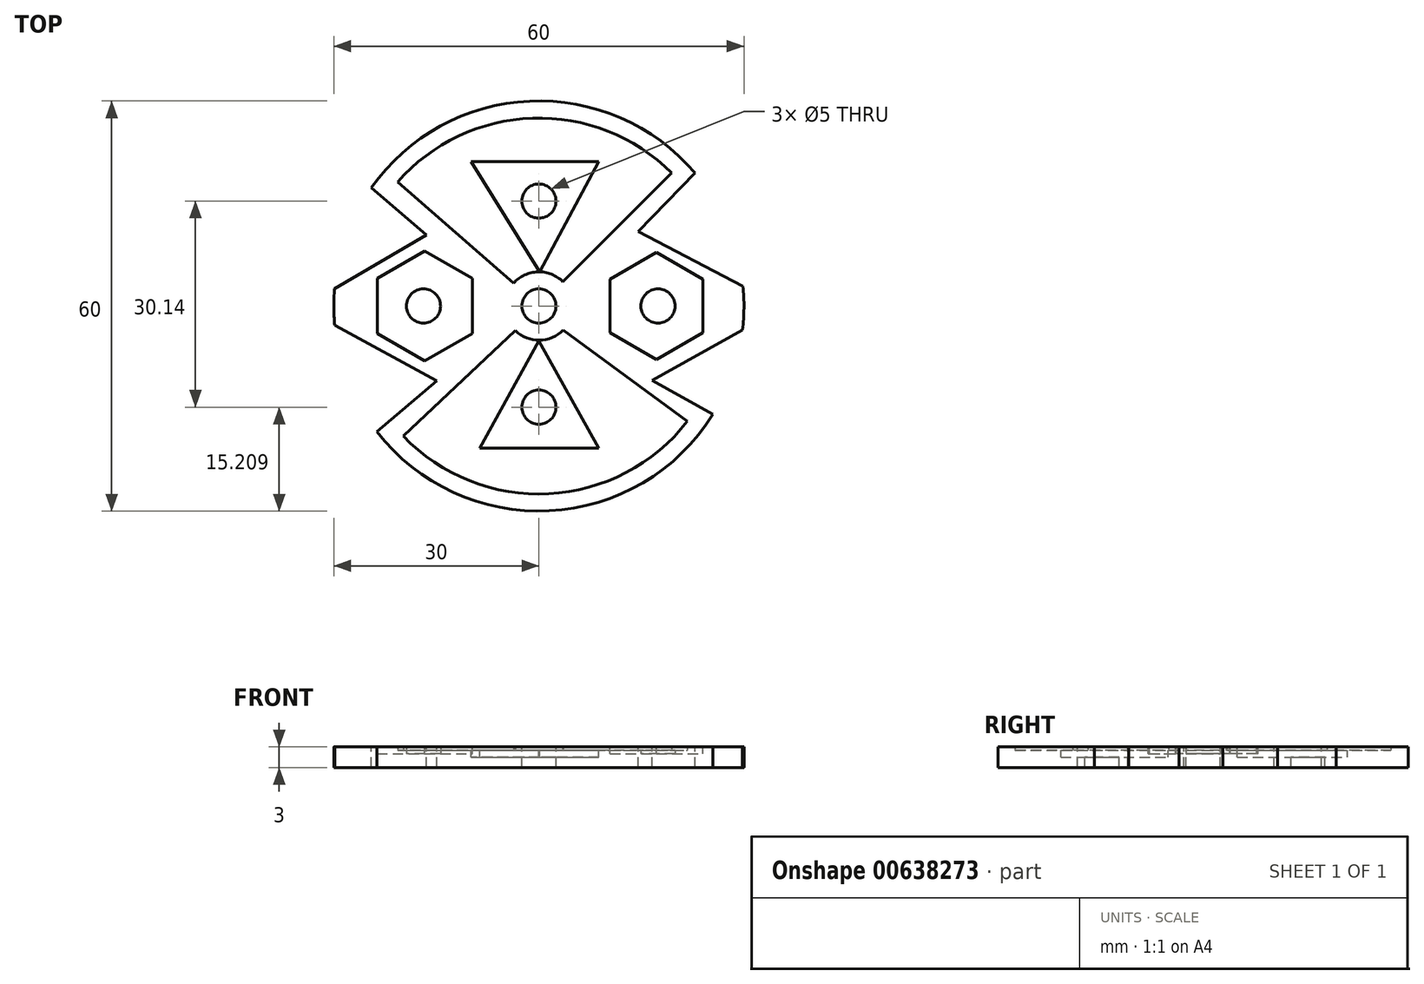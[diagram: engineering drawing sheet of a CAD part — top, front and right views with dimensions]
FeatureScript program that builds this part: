
annotation { "Feature Type Name" : "Feature", "Feature Type Description" : "" }
export const myFeature = defineFeature(function(context is Context, id is Id, definition is map)
    precondition{}
    {
        {
            var Q0;
            Q0=qCreatedBy(makeId("Top.planeOp"),FACE);
            var sketch = newSketch(context, id + "F0", { "sketchPlane" : qUnion([Q0])});
            skCircle(sketch, "E0", {"center": v(0, 0) * mm, "radius": 30 * mm});
            skSolve(sketch);
        }
        {
            var Q0;
            Q0=makeQuery(id+"F0.imprint","IMPRINT",FACE,{"disambiguationData":[TD([[makeQuery(id+"F0.imprint","IMPRINT",EDGE,{"derivedFrom":sQuery(id+"F0.wireOp",EDGE,"E0")}),1.0]])]});
            extrude(context, id + "F1", {"entities" : qUnion([Q0]), "depth" : 3 * mm, "offsetDistance" : 25 * mm});
        }
        {
            var Q0;
            Q0=makeQuery(id+"F1.opExtrude","CAP_FACE",FACE,{"disambiguationData":[OSD([sQuery(id+"F0.wireOp",EDGE,"E0")])],"isStart":false});
            var sketch = newSketch(context, id + "F2", { "sketchPlane" : qUnion([Q0])});
            skCircle(sketch, "E1", {"center": v(0, 0) * mm, "radius": 2.5 * mm});
            skSolve(sketch);
        }
        {
            var Q0;
            Q0=sQuery(id+"F2.wireOp",VERTEX,"E1.center");
            var Q1;
            Q1=makeQuery(id+"F1.opExtrude","SWEPT_BODY",BODY,{"disambiguationData":[OSD([sQuery(id+"F0.wireOp",EDGE,"E0")])]});
            hole(context, id + "F3", {"style" : HoleStyle.SIMPLE, "endStyle" : HoleEndStyle.THROUGH, "holeDiameter" : 5 * mm, "majorDiameter" : 5 * mm, "isTappedThrough" : true, "tappedDepth" : 12 * mm, "tapClearance" : 3, "locations" : qUnion([Q0]), "scope" : qUnion([Q1])});
        }
        {
            var Q0;
            Q0=makeQuery(id+"F1.opExtrude","CAP_FACE",FACE,{"disambiguationData":[OSD([sQuery(id+"F0.wireOp",EDGE,"E0")])],"isStart":false});
            shell(context, id + "F4", {"entities" : qUnion([Q0]), "thickness" : 2.5 * mm});
        }
        {
            var Q0;
            {var subQ0=sQuery(id+"F0.wireOp",EDGE,"E0");Q0=makeQuery(id+"F4.opShell","OFFSET_FACE",FACE,{"disambiguationData":[OSD([subQ0]),TDD([makeQuery(id+"F1.opExtrude","CAP_FACE",FACE,{"disambiguationData":[OSD([subQ0])],"isStart":true})])]});}
            var sketch = newSketch(context, id + "F5", { "sketchPlane" : qUnion([Q0])});
            skLineSegment(sketch, "E2", {"start": v(-20.67, 18.14) * mm, "end": v(-3.7, 3.36) * mm});
            skLineSegment(sketch, "E3", {"start": v(3.51, 3.56) * mm, "end": v(19.42, 19.48) * mm});
            skLineSegment(sketch, "E4", {"start": v(-3.47, -3.6) * mm, "end": v(-19.84, -19.04) * mm});
            skLineSegment(sketch, "E5", {"start": v(3.58, -3.5) * mm, "end": v(21.73, -16.86) * mm});
            skSolve(sketch);
        }
        {
            var Q0;
            {var subQ0=sQuery(id+"F5.wireOp",EDGE,"E2");Q0=makeQuery(id+"F5.imprint","IMPRINT",FACE,{"disambiguationData":[TD([[makeQuery(id+"F5.imprint","IMPRINT",EDGE,{"derivedFrom":subQ0}),-1.0]])]});}
            var Q1;
            {var subQ0=sQuery(id+"F5.wireOp",EDGE,"E3");Q1=makeQuery(id+"F5.imprint","IMPRINT",FACE,{"disambiguationData":[TD([[makeQuery(id+"F5.imprint","IMPRINT",EDGE,{"derivedFrom":subQ0}),-1.0]])]});}
            extrude(context, id + "F6", {"entities" : qUnion([Q0, Q1]), "operationType" : NewBodyOperationType.ADD, "depth" : 0.5 * mm, "offsetDistance" : 25 * mm});
        }
        {
            var Q0;
            {var subQ0=sQuery(id+"F3.hole-0.sketch.wireOp",EDGE,"core_line_2");var subQ1=sQuery(id+"F0.wireOp",EDGE,"E0");var subQ2=makeQuery(id+"F1.opExtrude","CAP_FACE",FACE,{"disambiguationData":[OSD([subQ1])],"isStart":false});Q0=makeQuery(id+"F6.boolean.opBoolean","MERGE",FACE,{"derivedFrom":[makeQuery(id+"F4.opShell","OFFSET_FACE",FACE,{"disambiguationData":[OSD([subQ1]),TDD([subQ2])]}),subQ2,makeQuery(id+"F6.opExtrude","CAP_FACE",FACE,{"disambiguationData":[OSD([subQ1,subQ0,sQuery(id+"F5.wireOp",EDGE,"E2"),sQuery(id+"F5.wireOp",EDGE,"E4")])],"isStart":false}),makeQuery(id+"F6.opExtrude","CAP_FACE",FACE,{"disambiguationData":[OSD([subQ1,subQ0,sQuery(id+"F5.wireOp",EDGE,"E3"),sQuery(id+"F5.wireOp",EDGE,"E5")])],"isStart":false})]});}
            var sketch = newSketch(context, id + "F7", { "sketchPlane" : qUnion([Q0])});
            skCircle(sketch, "E6.cCircle", {"center": v(-16.7, 0) * mm, "radius": 6.96 * mm, "construction": true});
            skLineSegment(sketch, "E6.0", {"start": v(-9.75, 4.02) * mm, "end": v(-9.75, -4.02) * mm});
            skLineSegment(sketch, "E6.1", {"start": v(-9.75, -4.02) * mm, "end": v(-16.7, -8.03) * mm});
            skLineSegment(sketch, "E6.2", {"start": v(-16.7, -8.03) * mm, "end": v(-23.66, -4.02) * mm});
            skLineSegment(sketch, "E6.3", {"start": v(-23.66, -4.02) * mm, "end": v(-23.66, 4.02) * mm});
            skLineSegment(sketch, "E6.4", {"start": v(-23.66, 4.02) * mm, "end": v(-16.7, 8.03) * mm});
            skLineSegment(sketch, "E6.5", {"start": v(-16.7, 8.03) * mm, "end": v(-9.75, 4.02) * mm});
            skPoint(sketch, "E6.0.midPoint", {"position": v(-9.75, 0) * mm});
            skCircle(sketch, "E7.cCircle", {"center": v(17.2, 0) * mm, "radius": 6.78 * mm, "construction": true});
            skLineSegment(sketch, "E7.0", {"start": v(23.98, 3.91) * mm, "end": v(23.98, -3.91) * mm});
            skLineSegment(sketch, "E7.1", {"start": v(23.98, -3.91) * mm, "end": v(17.2, -7.83) * mm});
            skLineSegment(sketch, "E7.2", {"start": v(17.2, -7.83) * mm, "end": v(10.42, -3.91) * mm});
            skLineSegment(sketch, "E7.3", {"start": v(10.42, -3.91) * mm, "end": v(10.42, 3.91) * mm});
            skLineSegment(sketch, "E7.4", {"start": v(10.42, 3.91) * mm, "end": v(17.2, 7.83) * mm});
            skLineSegment(sketch, "E7.5", {"start": v(17.2, 7.83) * mm, "end": v(23.98, 3.91) * mm});
            skPoint(sketch, "E7.0.midPoint", {"position": v(23.98, 0) * mm});
            skSolve(sketch);
        }
        {
            var Q0;
            Q0=makeQuery(id+"F7.imprint","IMPRINT",FACE,{"disambiguationData":[TD([[makeQuery(id+"F7.imprint","IMPRINT",EDGE,{"derivedFrom":sQuery(id+"F7.wireOp",EDGE,"E6.0")}),-1.0]])]});
            var Q1;
            Q1=makeQuery(id+"F7.imprint","IMPRINT",FACE,{"disambiguationData":[TD([[makeQuery(id+"F7.imprint","IMPRINT",EDGE,{"derivedFrom":sQuery(id+"F7.wireOp",EDGE,"E7.0")}),-1.0]])]});
            extrude(context, id + "F8", {"entities" : qUnion([Q0, Q1]), "operationType" : NewBodyOperationType.REMOVE, "oppositeDirection" : true, "depth" : 1 * mm, "offsetDistance" : 25 * mm});
        }
        {
            var Q0;
            Q0=makeQuery(id+"F8.boolean.opBoolean","COPY",FACE,{"derivedFrom":makeQuery(id+"F8.opExtrude","CAP_FACE",FACE,{"disambiguationData":[OSD([sQuery(id+"F7.wireOp",EDGE,"E6.0"),sQuery(id+"F7.wireOp",EDGE,"E6.1"),sQuery(id+"F7.wireOp",EDGE,"E6.2"),sQuery(id+"F7.wireOp",EDGE,"E6.3"),sQuery(id+"F7.wireOp",EDGE,"E6.4"),sQuery(id+"F7.wireOp",EDGE,"E6.5")])],"isStart":false})});
            var sketch = newSketch(context, id + "F9", { "sketchPlane" : qUnion([Q0])});
            skCircle(sketch, "E8", {"center": v(-16.88, 0) * mm, "radius": 2.5 * mm});
            skSolve(sketch);
        }
        {
            var Q0;
            Q0=makeQuery(id+"F9.imprint","IMPRINT",FACE,{"disambiguationData":[TD([[makeQuery(id+"F9.imprint","IMPRINT",EDGE,{"derivedFrom":sQuery(id+"F9.wireOp",EDGE,"E8")}),1.0]])]});
            extrude(context, id + "F10", {"entities" : qUnion([Q0]), "operationType" : NewBodyOperationType.ADD, "depth" : 1 * mm, "offsetDistance" : 25 * mm});
        }
        {
            var Q0;
            Q0=makeQuery(id+"F8.boolean.opBoolean","COPY",FACE,{"derivedFrom":makeQuery(id+"F8.opExtrude","CAP_FACE",FACE,{"disambiguationData":[OSD([sQuery(id+"F7.wireOp",EDGE,"E7.0"),sQuery(id+"F7.wireOp",EDGE,"E7.1"),sQuery(id+"F7.wireOp",EDGE,"E7.2"),sQuery(id+"F7.wireOp",EDGE,"E7.3"),sQuery(id+"F7.wireOp",EDGE,"E7.4"),sQuery(id+"F7.wireOp",EDGE,"E7.5")])],"isStart":false})});
            var sketch = newSketch(context, id + "F11", { "sketchPlane" : qUnion([Q0])});
            skCircle(sketch, "E9", {"center": v(17.42, 0) * mm, "radius": 2.5 * mm});
            skSolve(sketch);
        }
        {
            var Q0;
            Q0=makeQuery(id+"F11.imprint","IMPRINT",FACE,{"disambiguationData":[TD([[makeQuery(id+"F11.imprint","IMPRINT",EDGE,{"derivedFrom":sQuery(id+"F11.wireOp",EDGE,"E9")}),1.0]])]});
            extrude(context, id + "F12", {"entities" : qUnion([Q0]), "operationType" : NewBodyOperationType.ADD, "depth" : 0.5 * mm, "offsetDistance" : 25 * mm});
        }
        {
            var Q0;
            {var subQ0=sQuery(id+"F3.hole-0.sketch.wireOp",EDGE,"core_line_2");var subQ1=sQuery(id+"F0.wireOp",EDGE,"E0");var subQ2=makeQuery(id+"F1.opExtrude","CAP_FACE",FACE,{"disambiguationData":[OSD([subQ1])],"isStart":false});Q0=makeQuery(id+"F6.boolean.opBoolean","MERGE",FACE,{"derivedFrom":[makeQuery(id+"F4.opShell","OFFSET_FACE",FACE,{"disambiguationData":[OSD([subQ1]),TDD([subQ2])]}),subQ2,makeQuery(id+"F6.opExtrude","CAP_FACE",FACE,{"disambiguationData":[OSD([subQ1,subQ0,sQuery(id+"F5.wireOp",EDGE,"E2"),sQuery(id+"F5.wireOp",EDGE,"E4")])],"isStart":false}),makeQuery(id+"F6.opExtrude","CAP_FACE",FACE,{"disambiguationData":[OSD([subQ1,subQ0,sQuery(id+"F5.wireOp",EDGE,"E3"),sQuery(id+"F5.wireOp",EDGE,"E5")])],"isStart":false})]});}
            var sketch = newSketch(context, id + "F13", { "sketchPlane" : qUnion([Q0])});
            skLineSegment(sketch, "E10", {"start": v(-24.5, 17.3) * mm, "end": v(-16.47, 10.4) * mm});
            skLineSegment(sketch, "E11", {"start": v(-16.47, 10.4) * mm, "end": v(-29.9, 2.53) * mm});
            skLineSegment(sketch, "E12", {"start": v(-23.72, -18.36) * mm, "end": v(-14.93, -10.97) * mm});
            skLineSegment(sketch, "E13", {"start": v(-14.93, -10.97) * mm, "end": v(-29.87, -2.81) * mm});
            skLineSegment(sketch, "E14", {"start": v(22.82, 19.48) * mm, "end": v(14.54, 10.89) * mm});
            skLineSegment(sketch, "E15", {"start": v(14.54, 10.89) * mm, "end": v(29.86, 2.9) * mm});
            skLineSegment(sketch, "E16", {"start": v(25.46, -15.86) * mm, "end": v(16.56, -10.88) * mm});
            skLineSegment(sketch, "E17", {"start": v(16.56, -10.88) * mm, "end": v(29.8, -3.5) * mm});
            skSolve(sketch);
        }
        {
            var Q0;
            {var subQ0=sQuery(id+"F13.wireOp",EDGE,"E10");Q0=makeQuery(id+"F13.imprint","IMPRINT",FACE,{"disambiguationData":[TD([[makeQuery(id+"F13.imprint","IMPRINT",EDGE,{"derivedFrom":subQ0}),-1.0]])]});}
            var Q1;
            {var subQ0=sQuery(id+"F13.wireOp",EDGE,"E12");Q1=makeQuery(id+"F13.imprint","IMPRINT",FACE,{"disambiguationData":[TD([[makeQuery(id+"F13.imprint","IMPRINT",EDGE,{"derivedFrom":subQ0}),1.0]])]});}
            var Q2;
            {var subQ0=sQuery(id+"F13.wireOp",EDGE,"E14");Q2=makeQuery(id+"F13.imprint","IMPRINT",FACE,{"disambiguationData":[TD([[makeQuery(id+"F13.imprint","IMPRINT",EDGE,{"derivedFrom":subQ0}),1.0]])]});}
            var Q3;
            {var subQ0=sQuery(id+"F13.wireOp",EDGE,"E16");Q3=makeQuery(id+"F13.imprint","IMPRINT",FACE,{"disambiguationData":[TD([[makeQuery(id+"F13.imprint","IMPRINT",EDGE,{"derivedFrom":subQ0}),-1.0]])]});}
            extrude(context, id + "F14", {"entities" : qUnion([Q0, Q1, Q2, Q3]), "operationType" : NewBodyOperationType.REMOVE, "oppositeDirection" : true, "depth" : 25 * mm, "offsetDistance" : 25 * mm});
        }
        {
            var Q0;
            {var subQ0=sQuery(id+"F0.wireOp",EDGE,"E0");Q0=makeQuery(id+"F6.boolean.opBoolean","SPLIT",FACE,{"disambiguationData":[TD([makeQuery(id+"F6.opExtrude","SWEPT_FACE",FACE,{"disambiguationData":[OSD([sQuery(id+"F5.wireOp",EDGE,"E2")])]})])],"derivedFrom":makeQuery(id+"F4.opShell","OFFSET_FACE",FACE,{"disambiguationData":[OSD([subQ0]),TDD([makeQuery(id+"F1.opExtrude","CAP_FACE",FACE,{"disambiguationData":[OSD([subQ0])],"isStart":true})])]})});}
            var sketch = newSketch(context, id + "F15", { "sketchPlane" : qUnion([Q0])});
            skLineSegment(sketch, "E18", {"start": v(0.14, 5) * mm, "end": v(-9.92, 21.1) * mm});
            skPoint(sketch, "E18.startSnap0", {"position": v(-0.14, 5) * mm});
            skLineSegment(sketch, "E19", {"start": v(-9.92, 21.1) * mm, "end": v(6.93, 21.1) * mm});
            skLineSegment(sketch, "E20", {"start": v(6.93, 21.1) * mm, "end": v(8.76, 21.1) * mm});
            skLineSegment(sketch, "E21", {"start": v(8.76, 21.1) * mm, "end": v(0.14, 5) * mm});
            skLineSegment(sketch, "E22", {"start": v(0, -5.1) * mm, "end": v(-8.67, -20.8) * mm});
            skLineSegment(sketch, "E23", {"start": v(-8.67, -20.8) * mm, "end": v(8, -20.8) * mm});
            skLineSegment(sketch, "E24", {"start": v(8, -20.8) * mm, "end": v(8.76, -20.8) * mm});
            skLineSegment(sketch, "E25", {"start": v(8.76, -20.8) * mm, "end": v(0, -5.1) * mm});
            skSolve(sketch);
        }
        {
            var Q0;
            Q0=makeQuery(id+"F15.imprint","IMPRINT",FACE,{"disambiguationData":[TD([[makeQuery(id+"F15.imprint","IMPRINT",EDGE,{"derivedFrom":sQuery(id+"F15.wireOp",EDGE,"E18")}),-1.0]])]});
            var Q1;
            Q1=makeQuery(id+"F15.imprint","IMPRINT",FACE,{"disambiguationData":[TD([[makeQuery(id+"F15.imprint","IMPRINT",EDGE,{"derivedFrom":sQuery(id+"F15.wireOp",EDGE,"E22")}),1.0]])]});
            extrude(context, id + "F16", {"entities" : qUnion([Q0, Q1]), "operationType" : NewBodyOperationType.REMOVE, "oppositeDirection" : true, "depth" : 1 * mm, "offsetDistance" : 25 * mm});
        }
        {
            var Q0;
            Q0=makeQuery(id+"F16.boolean.opBoolean","COPY",FACE,{"derivedFrom":makeQuery(id+"F16.opExtrude","CAP_FACE",FACE,{"disambiguationData":[OSD([sQuery(id+"F15.wireOp",EDGE,"E18"),sQuery(id+"F15.wireOp",EDGE,"E19"),sQuery(id+"F15.wireOp",EDGE,"E20"),sQuery(id+"F15.wireOp",EDGE,"E21")])],"isStart":false})});
            var sketch = newSketch(context, id + "F17", { "sketchPlane" : qUnion([Q0])});
            skCircle(sketch, "E26", {"center": v(0, 15.35) * mm, "radius": 2.5 * mm});
            skSolve(sketch);
        }
        {
            var Q0;
            Q0=makeQuery(id+"F17.imprint","IMPRINT",FACE,{"disambiguationData":[TD([[makeQuery(id+"F17.imprint","IMPRINT",EDGE,{"derivedFrom":sQuery(id+"F17.wireOp",EDGE,"E26")}),1.0]])]});
            extrude(context, id + "F18", {"entities" : qUnion([Q0]), "operationType" : NewBodyOperationType.REMOVE, "oppositeDirection" : true, "depth" : 25 * mm, "offsetDistance" : 25 * mm});
        }
        {
            var Q0;
            Q0=makeQuery(id+"F16.boolean.opBoolean","COPY",FACE,{"derivedFrom":makeQuery(id+"F16.opExtrude","CAP_FACE",FACE,{"disambiguationData":[OSD([sQuery(id+"F15.wireOp",EDGE,"E22"),sQuery(id+"F15.wireOp",EDGE,"E23"),sQuery(id+"F15.wireOp",EDGE,"E24"),sQuery(id+"F15.wireOp",EDGE,"E25")])],"isStart":false})});
            var sketch = newSketch(context, id + "F19", { "sketchPlane" : qUnion([Q0])});
            skCircle(sketch, "E27", {"center": v(0, -14.8) * mm, "radius": 2.5 * mm});
            skSolve(sketch);
        }
        {
            var Q0;
            Q0=makeQuery(id+"F19.imprint","IMPRINT",FACE,{"disambiguationData":[TD([[makeQuery(id+"F19.imprint","IMPRINT",EDGE,{"derivedFrom":sQuery(id+"F19.wireOp",EDGE,"E27")}),1.0]])]});
            extrude(context, id + "F20", {"entities" : qUnion([Q0]), "operationType" : NewBodyOperationType.REMOVE, "oppositeDirection" : true, "depth" : 25 * mm, "offsetDistance" : 25 * mm});
        }
    });
